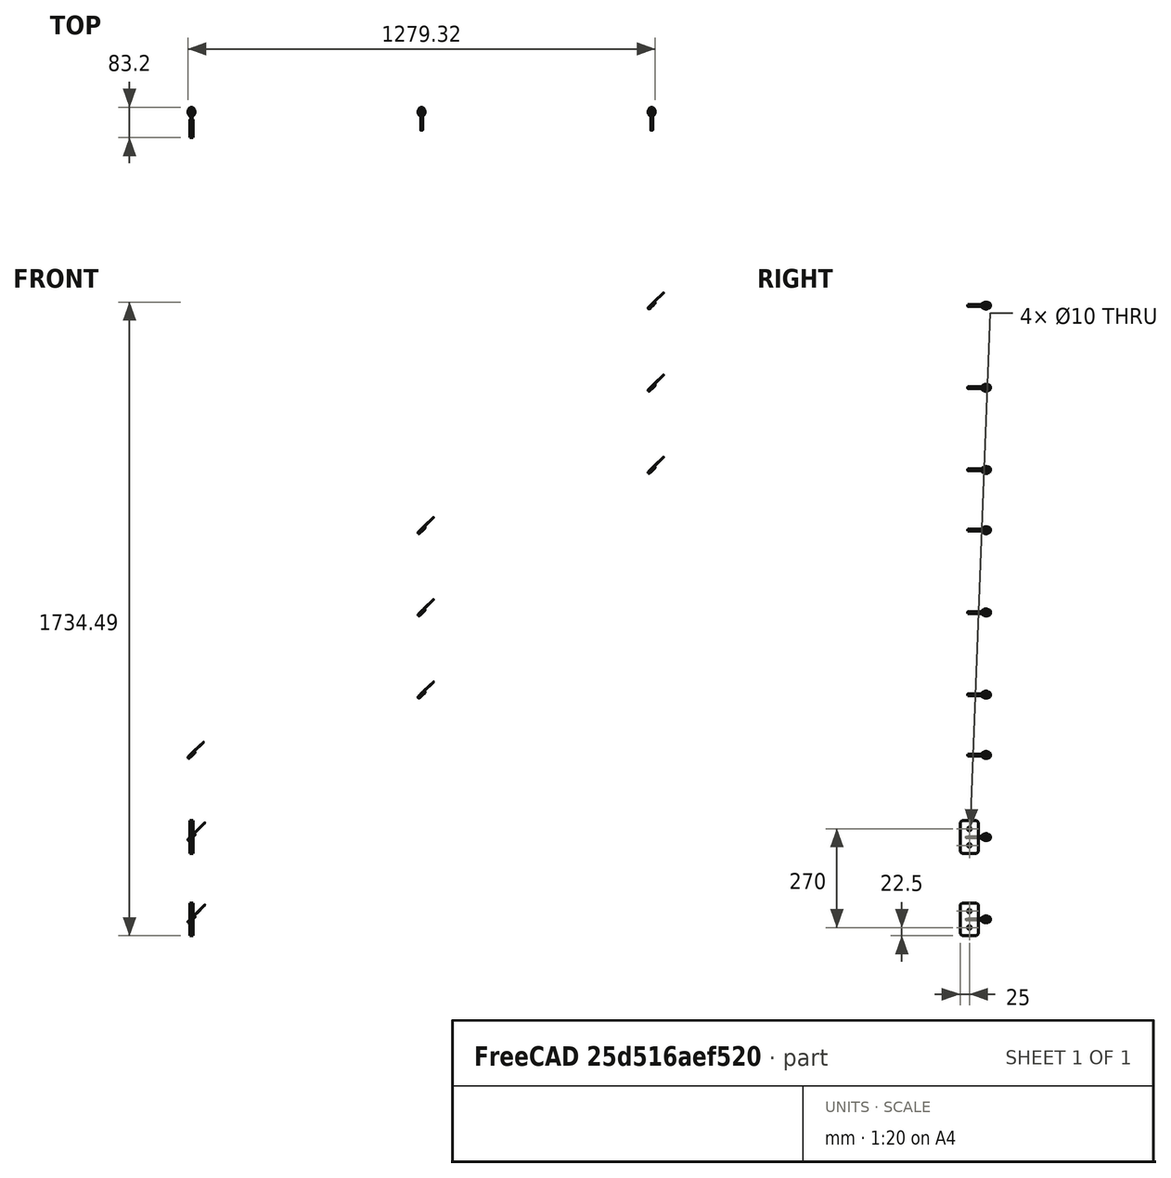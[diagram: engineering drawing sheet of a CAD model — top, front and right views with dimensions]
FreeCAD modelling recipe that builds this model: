
FCSTD DOCUMENT  (FreeCAD 0.17R10993 (Git))
Label: railing_dist
License: All rights reserved
LicenseURL: http://en.wikipedia.org/wiki/All_rights_reserved
objects: Part::FeaturePython×4, TechDraw::DrawProjGroupItem×4, Part::Part2DObjectPython×3, Part::Extrusion×3, Part::Chamfer×1, Part::Compound×1, Part::Cut×1, App::DocumentObjectGroup×1, TechDraw::DrawSVGTemplate×1, TechDraw::DrawProjGroup×1, TechDraw::DrawViewPart×1, TechDraw::DrawPage×1
note: 13 computed .brp shape members not serialized (recipe doc carries the construction recipe); baked Part::Feature solids carry a one-line shape summary decoded from their .brp

FEATURE [Part::Part2DObjectPython] Circle  # Draft 2D object (typed FeaturePython)
  FirstAngle = 0
  LastAngle = 0
  MakeFace = true
  Placement = pos=(64.3902,-411,100) rot=(0.57735,-0.57735,-0.57735;2.0944rad)
  Radius = 5
FEATURE [Part::Extrusion] Extrude
  Base = -> Circle
  Dir = (1,0,0)
  DirMode = 0
  FaceMakerClass = Part::FaceMakerBullseye
  LengthFwd = 80
  LengthRev = 0
  Placement = pos=(25,0,0) rot=(0,0,1;0rad)
  Solid = false
  Symmetric = true
FEATURE [Part::FeaturePython] Array  # Draft array (typed FeaturePython)
  Angle = 360
  ArrayType = 0
  Axis = (0,0,1)
  Base = -> Extrude
  Center = (0,0,0)
  Fuse = false
  IntervalAxis = (0,0,0)
  IntervalX = (0,0,45)
  IntervalY = (0,0,225)
  IntervalZ = (0,0,0)
  NumberPolar = 1
  NumberX = 2
  NumberY = 5
  NumberZ = 1
  Placement = pos=(0,0,-27.5) rot=(0,0,1;0rad)
FEATURE [Part::Part2DObjectPython] Rectangle  # Draft 2D object (typed FeaturePython)
  ChamferSize = 0
  Columns = 1
  FilletRadius = 0
  Height = 50
  Length = 10
  MakeFace = true
  Placement = pos=(84.3902,-436,432.5) rot=(0,0,1;0rad)
  Rows = 1
FEATURE [Part::Extrusion] Extrude005
  Base = -> Rectangle
  Dir = (0,0,1)
  DirMode = 0
  FaceMakerClass = Part::FaceMakerBullseye
  LengthFwd = 90
  LengthRev = 0
  Placement = pos=(0,0,67.5) rot=(0,0,1;0rad)
  Solid = false
  Symmetric = false
FEATURE [Part::Chamfer] Chamfer001
  Base = -> Extrude005
  Edges = 4 edges r=5: [Edge3,Edge4,Edge9,Edge10]
FEATURE [Part::FeaturePython] Array002  # Draft array (typed FeaturePython)
  Angle = 360
  ArrayType = 0
  Axis = (0,0,1)
  Base = -> Chamfer001
  Center = (0,0,0)
  Fuse = false
  IntervalAxis = (0,0,0)
  IntervalX = (0,0,225)
  IntervalY = (0,1,0)
  IntervalZ = (0,0,0)
  NumberPolar = 1
  NumberX = 2
  NumberY = 1
  NumberZ = 1
FEATURE [Part::FeaturePython] railing_eyelet_01  # a2plus imported part (geometry in sourceFile) (typed FeaturePython)
  fixedPosition = true
  sourceFile = railing_eyelet.fcstd
  timeLastImport = 1.49443e+09
  updateColors = true
FEATURE [Part::Part2DObjectPython] Circle001  # Draft 2D object (typed FeaturePython)
  FirstAngle = 0
  LastAngle = 0
  MakeFace = true
  Placement = pos=(89.3902,-420.3,545) rot=(1,0,0;1.5708rad)
  Radius = 2.5
  Support = -> [railing_eyelet_01]
FEATURE [Part::Extrusion] Extrude006
  Base = -> Circle001
  Dir = (0,1,0)
  DirMode = 0
  FaceMakerClass = Part::FaceMakerBullseye
  LengthFwd = 35
  LengthRev = 0
  Solid = false
  Symmetric = false
FEATURE [Part::FeaturePython] Array006  # Draft array (typed FeaturePython)
  Angle = 360
  ArrayType = 0
  Axis = (0,0,1)
  Base = -> Extrude006
  Center = (0,0,0)
  Fuse = false
  IntervalAxis = (0,0,0)
  IntervalX = (0,0,225)
  IntervalY = (0,0,0)
  IntervalZ = (0,0,0)
  NumberPolar = 1
  NumberX = 3
  NumberY = 0
  NumberZ = 1
FEATURE [Part::Compound] Compound
  Links = -> [Array006,Array]
FEATURE [Part::Cut] Cut002  label="plates"
  Base = -> Array002
  Tool = -> Compound
FEATURE [App::DocumentObjectGroup] Group  label="ref"
  Group = -> [railing_eyelet_01]
FEATURE [TechDraw::DrawSVGTemplate] Template
  Height = 841
  Orientation = 0
  Width = 594
FEATURE [TechDraw::DrawProjGroupItem] ProjItem  label="Front"
  ArcCenterMarks = true
  CenterScale = 2
  Direction = (0,-1,0)
  HardHidden = true
  HiddenWidth = 0.15
  HorizCenterLine = false
  IsoCount = 0
  IsoHidden = false
  IsoVisible = false
  IsoWidth = 0.3
  KeepLabel = false
  LineWidth = 0.7
  Rotation = 0
  RotationVector = (1,0,0)
  Scale = 0.5
  ScaleType = 2
  SeamHidden = false
  SeamVisible = false
  ShowSectionLine = true
  SmoothHidden = false
  SmoothVisible = false
  Source = -> Cut002
  Type = 0
  VertCenterLine = false
  X = -30
  Y = 20
FEATURE [TechDraw::DrawProjGroupItem] ProjItem001  label="Left"
  ArcCenterMarks = true
  CenterScale = 2
  Direction = (-1,0,0)
  HardHidden = true
  HiddenWidth = 0.15
  HorizCenterLine = false
  IsoCount = 0
  IsoHidden = false
  IsoVisible = false
  IsoWidth = 0.3
  KeepLabel = false
  LineWidth = 0.7
  Rotation = 0
  RotationVector = (0,1,0)
  Scale = 0.5
  ScaleType = 2
  SeamHidden = false
  SeamVisible = false
  ShowSectionLine = true
  SmoothHidden = false
  SmoothVisible = false
  Source = -> Cut002
  Type = 1
  VertCenterLine = false
  X = 50
  Y = 0
FEATURE [TechDraw::DrawProjGroupItem] ProjItem002  label="Rear"
  ArcCenterMarks = true
  CenterScale = 2
  Direction = (0,1,0)
  HardHidden = true
  HiddenWidth = 0.15
  HorizCenterLine = false
  IsoCount = 0
  IsoHidden = false
  IsoVisible = false
  IsoWidth = 0.3
  KeepLabel = false
  LineWidth = 0.7
  Rotation = 0
  RotationVector = (-1,0,0)
  Scale = 0.5
  ScaleType = 2
  SeamHidden = false
  SeamVisible = false
  ShowSectionLine = true
  SmoothHidden = false
  SmoothVisible = false
  Source = -> Cut002
  Type = 3
  VertCenterLine = false
  X = 100
  Y = 0
FEATURE [TechDraw::DrawProjGroupItem] ProjItem003  label="Top"
  ArcCenterMarks = true
  CenterScale = 2
  Direction = (0,0,1)
  HardHidden = true
  HiddenWidth = 0.15
  HorizCenterLine = false
  IsoCount = 0
  IsoHidden = false
  IsoVisible = false
  IsoWidth = 0.3
  KeepLabel = false
  LineWidth = 0.7
  Rotation = 0
  RotationVector = (1,0,0)
  Scale = 0.5
  ScaleType = 2
  SeamHidden = false
  SeamVisible = false
  ShowSectionLine = true
  SmoothHidden = false
  SmoothVisible = false
  Source = -> Cut002
  Type = 4
  VertCenterLine = false
  X = 0
  Y = -132.5
FEATURE [TechDraw::DrawProjGroup] ProjGroup
  Anchor = -> ProjItem
  AutoDistribute = true
  KeepLabel = false
  ProjectionType = 0
  Rotation = 0
  Scale = 0.5
  ScaleType = 2
  Source = -> Cut002
  Views = -> [ProjItem,ProjItem001,ProjItem002,ProjItem003]
  X = 297
  Y = 420.5
  spacingX = 25
  spacingY = -25
FEATURE [TechDraw::DrawViewPart] View
  ArcCenterMarks = true
  CenterScale = 2
  Direction = (-0.45,-1,0.5)
  HardHidden = true
  HiddenWidth = 0.15
  HorizCenterLine = false
  IsoCount = 0
  IsoHidden = false
  IsoVisible = false
  IsoWidth = 0.3
  KeepLabel = false
  LineWidth = 0.7
  Rotation = 0
  Scale = 0.5
  ScaleType = 2
  SeamHidden = false
  SeamVisible = false
  ShowSectionLine = true
  SmoothHidden = false
  SmoothVisible = false
  Source = -> Cut002
  VertCenterLine = false
  X = 442.632
  Y = 413.796
FEATURE [TechDraw::DrawPage] Page
  ProjectionType = 0
  Template = -> Template
  Views = -> [ProjGroup,View]
